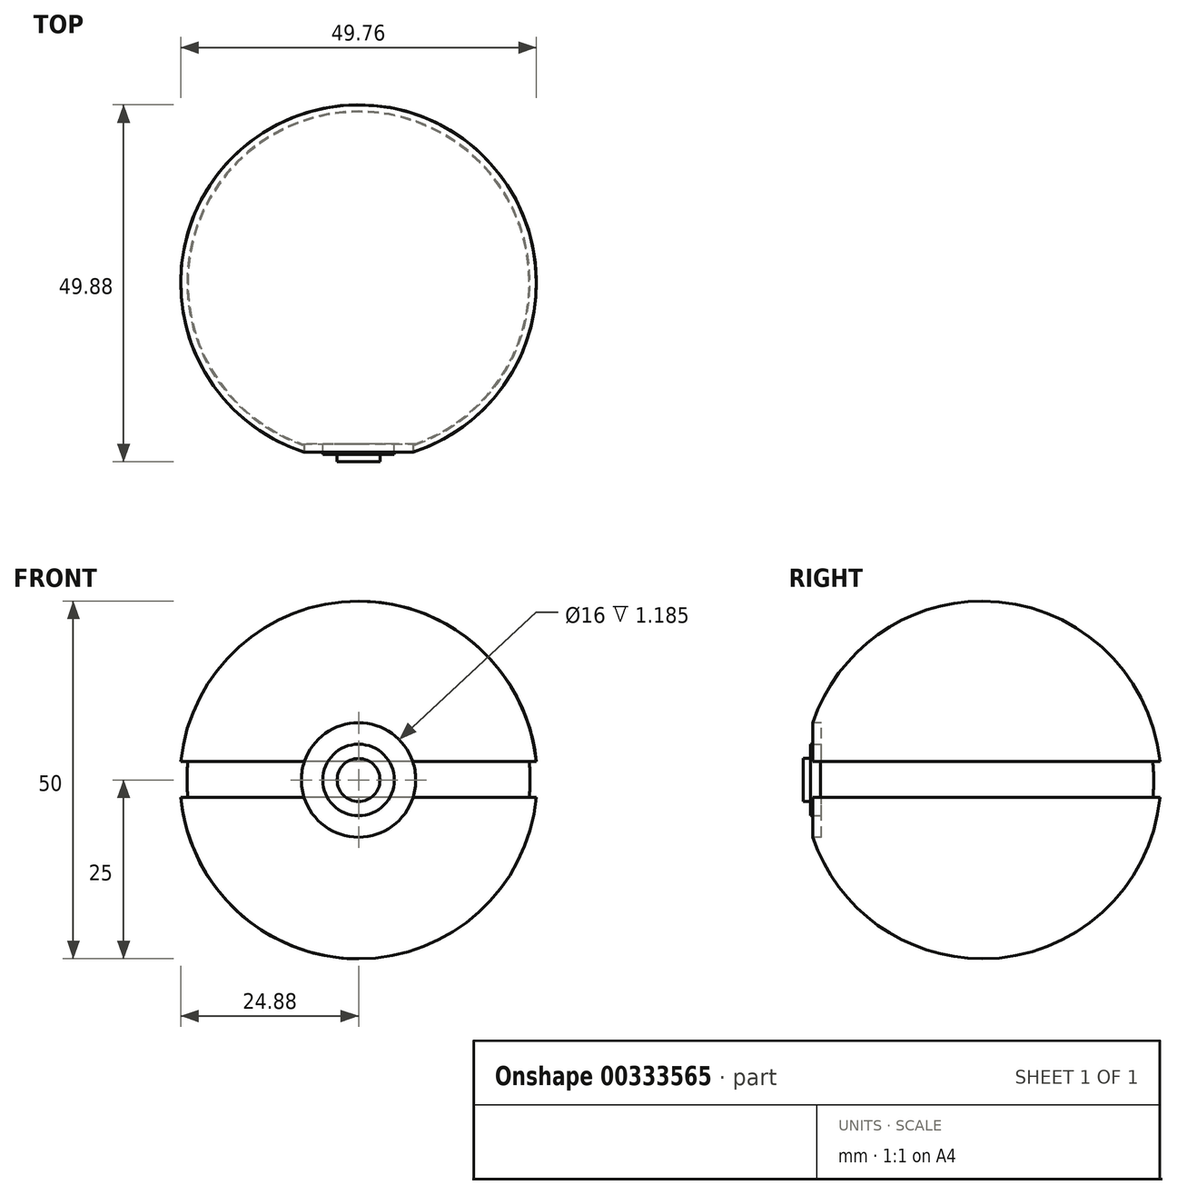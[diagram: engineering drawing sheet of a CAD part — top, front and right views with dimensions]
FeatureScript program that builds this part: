
annotation { "Feature Type Name" : "Feature", "Feature Type Description" : "" }
export const myFeature = defineFeature(function(context is Context, id is Id, definition is map)
    precondition{}
    {
        {
            var Q0;
            Q0=qCreatedBy(makeId("Front.planeOp"),FACE);
            var sketch = newSketch(context, id + "F0", { "sketchPlane" : qUnion([Q0])});
            skArc(sketch, "E0", {"start": v(0, 25) * mm, "mid": v(-16.74, 18.57) * mm, "end": v(-24.87, 2.58) * mm});
            skArc(sketch, "E1", {"start": v(-23.86, 2.58) * mm, "mid": v(-24, 0.09) * mm, "end": v(-23.88, -2.42) * mm});
            skLineSegment(sketch, "E2.bottom", {"start": v(-23.86, 2.58) * mm, "end": v(-24.87, 2.58) * mm});
            skLineSegment(sketch, "E2.top", {"start": v(-23.88, -2.42) * mm, "end": v(-24.88, -2.42) * mm});
            skLineSegment(sketch, "E3", {"start": v(0, 25) * mm, "end": v(0, -25) * mm});
            skArc(sketch, "E4.trimOffspring", {"start": v(-24.88, -2.42) * mm, "mid": v(-16.8, -18.51) * mm, "end": v(0, -25) * mm});
            skSolve(sketch);
        }
        {
            var Q0;
            Q0 = qSketchRegion(id + "F0", true);
            var Q1;
            Q1=sQuery(id+"F0.wireOp",EDGE,"E3");
            revolve(context, id + "F1", {"entities" : qUnion([Q0]), "axis" : qUnion([Q1]), "revolveType" : RevolveType.FULL});
        }
        {
            var Q0;
            Q0=qCreatedBy(makeId("Front.planeOp"),FACE);
            cPlane(context, id + "F2", {"entities" : qUnion([Q0]), "cplaneType" : CPlaneType.OFFSET, "offset" : 25 * mm, "width" : 150 * mm, "height" : 150 * mm});
        }
        {
            var Q0;
            Q0=qCreatedBy(id+"F2.planeOp",FACE);
            var sketch = newSketch(context, id + "F3", { "sketchPlane" : qUnion([Q0])});
            skCircle(sketch, "E5", {"center": v(0, 0) * mm, "radius": 8 * mm});
            skSolve(sketch);
        }
        {
            var Q0;
            Q0=makeQuery(id+"F3.imprint","IMPRINT",FACE,{"disambiguationData":[TD([[makeQuery(id+"F3.imprint","IMPRINT",EDGE,{"derivedFrom":sQuery(id+"F3.wireOp",EDGE,"E5")}),1.0]])]});
            extrude(context, id + "F4", {"entities" : qUnion([Q0]), "operationType" : NewBodyOperationType.REMOVE, "endBound" : BoundingType.SYMMETRIC, "oppositeDirection" : true, "depth" : 5 * mm});
        }
        {
            var Q0;
            Q0=qCreatedBy(makeId("Front.planeOp"),FACE);
            var sketch = newSketch(context, id + "F5", { "sketchPlane" : qUnion([Q0])});
            skCircle(sketch, "E6", {"center": v(0, 0) * mm, "radius": 5 * mm});
            skSolve(sketch);
        }
        {
            var Q0;
            Q0 = qSketchRegion(id + "F5", true);
            extrude(context, id + "F6", {"entities" : qUnion([Q0]), "operationType" : NewBodyOperationType.ADD, "depth" : 24 * mm});
        }
        {
            var Q0;
            Q0=qCreatedBy(makeId("Front.planeOp"),FACE);
            var sketch = newSketch(context, id + "F7", { "sketchPlane" : qUnion([Q0])});
            skCircle(sketch, "E7", {"center": v(0, 0) * mm, "radius": 3 * mm});
            skSolve(sketch);
        }
        {
            var Q0;
            Q0 = qSketchRegion(id + "F7", true);
            extrude(context, id + "F8", {"entities" : qUnion([Q0]), "operationType" : NewBodyOperationType.ADD, "depth" : 25 * mm});
        }
    });
